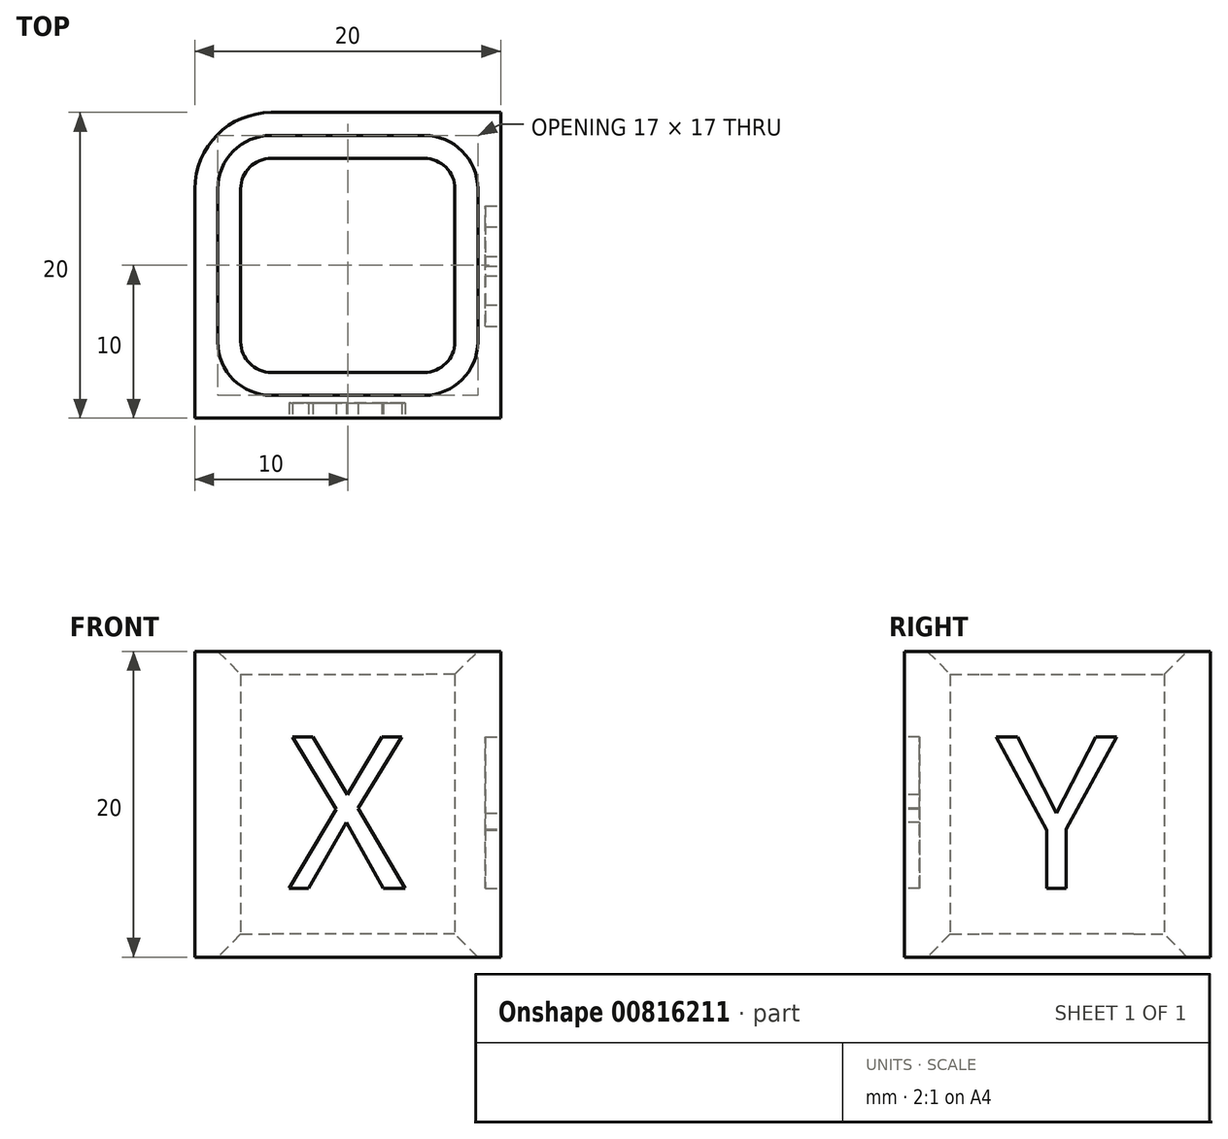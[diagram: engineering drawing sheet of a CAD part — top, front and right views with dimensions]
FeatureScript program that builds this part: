
annotation { "Feature Type Name" : "Feature", "Feature Type Description" : "" }
export const myFeature = defineFeature(function(context is Context, id is Id, definition is map)
    precondition{}
    {
        {
            var Q0;
            Q0=qCreatedBy(makeId("Top.planeOp"),FACE);
            var sketch = newSketch(context, id + "F0", { "sketchPlane" : qUnion([Q0])});
            skLineSegment(sketch, "E0.bottom", {"start": v(-10, 10) * mm, "end": v(10, 10) * mm});
            skLineSegment(sketch, "E0.top", {"start": v(-10, -10) * mm, "end": v(10, -10) * mm});
            skLineSegment(sketch, "E0.left", {"start": v(-10, 10) * mm, "end": v(-10, -10) * mm});
            skLineSegment(sketch, "E0.right", {"start": v(10, 10) * mm, "end": v(10, -10) * mm});
            skPoint(sketch, "E0.middle", {"position": v(0, 0) * mm});
            skLineSegment(sketch, "E1.bottom", {"start": v(5, -7) * mm, "end": v(-5, -7) * mm});
            skLineSegment(sketch, "E1.top", {"start": v(5, 7) * mm, "end": v(-5, 7) * mm});
            skLineSegment(sketch, "E1.left", {"start": v(7, -5) * mm, "end": v(7, 5) * mm});
            skLineSegment(sketch, "E1.right", {"start": v(-7, -5) * mm, "end": v(-7, 5) * mm});
            skPoint(sketch, "E2.visualSharp", {"position": v(-7, 7) * mm});
            skArc(sketch, "E2.filletArc", {"start": v(-5, 7) * mm, "mid": v(-6.41, 6.41) * mm, "end": v(-7, 5) * mm});
            skPoint(sketch, "E3.visualSharp", {"position": v(7, 7) * mm});
            skArc(sketch, "E3.filletArc", {"start": v(7, 5) * mm, "mid": v(6.41, 6.41) * mm, "end": v(5, 7) * mm});
            skPoint(sketch, "E4.visualSharp", {"position": v(7, -7) * mm});
            skArc(sketch, "E4.filletArc", {"start": v(5, -7) * mm, "mid": v(6.41, -6.41) * mm, "end": v(7, -5) * mm});
            skPoint(sketch, "E5.visualSharp", {"position": v(-7, -7) * mm});
            skArc(sketch, "E5.filletArc", {"start": v(-7, -5) * mm, "mid": v(-6.41, -6.41) * mm, "end": v(-5, -7) * mm});
            skSolve(sketch);
        }
        {
            var Q0;
            Q0=makeQuery(id+"F0.imprint","IMPRINT",FACE,{"disambiguationData":[TD([[makeQuery(id+"F0.imprint","IMPRINT",EDGE,{"derivedFrom":sQuery(id+"F0.wireOp",EDGE,"E0.bottom")}),-1.0]])]});
            extrude(context, id + "F1", {"entities" : qUnion([Q0]), "depth" : 20 * mm, "offsetDistance" : 25 * mm});
        }
        {
            var Q0;
            Q0=makeQuery(id+"F1.opExtrude","SWEPT_FACE",FACE,{"disambiguationData":[OSD([sQuery(id+"F0.wireOp",EDGE,"E0.top")])]});
            var sketch = newSketch(context, id + "F2", { "sketchPlane" : qUnion([Q0])});
            skText(sketch, "E6", { "text": "X", "fontName": "DroidSansMono.ttf"});
            const initialGuessF2  = {"E6": [-0.0042, 0.0045, 1, 0, 0.01]};
            skSetInitialGuess(sketch, initialGuessF2);
            skSolve(sketch);
        }
        {
            var Q0;
            Q0=makeQuery(id+"F1.opExtrude","SWEPT_FACE",FACE,{"disambiguationData":[OSD([sQuery(id+"F0.wireOp",EDGE,"E0.right")])]});
            var sketch = newSketch(context, id + "F3", { "sketchPlane" : qUnion([Q0])});
            skText(sketch, "E7", { "text": "Y", "fontName": "DroidSansMono.ttf"});
            const initialGuessF3  = {"E7": [-0.0042, 0.0045, 1, 0, 0.01]};
            skSetInitialGuess(sketch, initialGuessF3);
            skSolve(sketch);
        }
        {
            var Q0;
            Q0=makeQuery(id+"F2.imprint","IMPRINT",FACE,{"disambiguationData":[TD([[makeQuery(id+"F2.imprint","IMPRINT",EDGE,{"derivedFrom":sQuery(id+"F2.wireOp",EDGE,"E6.sketch_text.stroke-0")}),-1.0]])]});
            extrude(context, id + "F4", {"entities" : qUnion([Q0]), "operationType" : NewBodyOperationType.REMOVE, "oppositeDirection" : true, "depth" : 1 * mm, "offsetDistance" : 25 * mm});
        }
        {
            var Q0;
            Q0=makeQuery(id+"F3.imprint","IMPRINT",FACE,{"disambiguationData":[TD([[makeQuery(id+"F3.imprint","IMPRINT",EDGE,{"derivedFrom":sQuery(id+"F3.wireOp",EDGE,"E7.sketch_text.stroke-0")}),-1.0]])]});
            extrude(context, id + "F5", {"entities" : qUnion([Q0]), "operationType" : NewBodyOperationType.REMOVE, "oppositeDirection" : true, "depth" : 1 * mm, "offsetDistance" : 25 * mm});
        }
        {
            var Q0;
            Q0=makeQuery(id+"F1.opExtrude","SWEPT_EDGE",EDGE,{"disambiguationData":[OSD([sQuery(id+"F0.wireOp",EDGE,"E0.bottom"),sQuery(id+"F0.wireOp",EDGE,"E0.left")])]});
            fillet(context, id + "F6", {"entities" : qUnion([Q0]), "tangentPropagation" : true, "radius" : 5 * mm, "defaultsChanged" : false, "vertexSettings" : [], "allowEdgeOverflow" : false});
        }
        {
            var Q0;
            Q0=makeQuery(id+"F1.opExtrude","CAP_EDGE",EDGE,{"disambiguationData":[OSD([sQuery(id+"F0.wireOp",EDGE,"E2.filletArc")])],"isStart":false});
            var Q1;
            Q1=makeQuery(id+"F1.opExtrude","SWEPT_FACE",FACE,{"disambiguationData":[OSD([sQuery(id+"F0.wireOp",EDGE,"E2.filletArc")])]});
            var Q2;
            Q2=makeQuery(id+"F1.opExtrude","CAP_EDGE",EDGE,{"disambiguationData":[OSD([sQuery(id+"F0.wireOp",EDGE,"E5.filletArc")])],"isStart":false});
            var Q3;
            Q3=makeQuery(id+"F1.opExtrude","CAP_EDGE",EDGE,{"disambiguationData":[OSD([sQuery(id+"F0.wireOp",EDGE,"E4.filletArc")])],"isStart":false});
            var Q4;
            Q4=makeQuery(id+"F1.opExtrude","CAP_EDGE",EDGE,{"disambiguationData":[OSD([sQuery(id+"F0.wireOp",EDGE,"E1.bottom")])],"isStart":false});
            var Q5;
            Q5=makeQuery(id+"F1.opExtrude","CAP_EDGE",EDGE,{"disambiguationData":[OSD([sQuery(id+"F0.wireOp",EDGE,"E1.right")])],"isStart":false});
            var Q6;
            Q6=makeQuery(id+"F1.opExtrude","CAP_EDGE",EDGE,{"disambiguationData":[OSD([sQuery(id+"F0.wireOp",EDGE,"E1.top")])],"isStart":false});
            var Q7;
            Q7=makeQuery(id+"F1.opExtrude","CAP_EDGE",EDGE,{"disambiguationData":[OSD([sQuery(id+"F0.wireOp",EDGE,"E3.filletArc")])],"isStart":false});
            var Q8;
            Q8=makeQuery(id+"F1.opExtrude","CAP_EDGE",EDGE,{"disambiguationData":[OSD([sQuery(id+"F0.wireOp",EDGE,"E1.left")])],"isStart":false});
            chamfer(context, id + "F7", {"entities" : qUnion([Q0, Q1, Q2, Q3, Q4, Q5, Q6, Q7, Q8]), "width" : 1.5 * mm, "tangentPropagation" : true});
        }
    });
